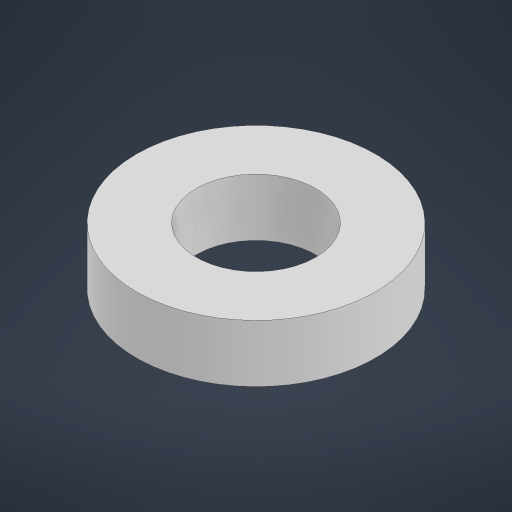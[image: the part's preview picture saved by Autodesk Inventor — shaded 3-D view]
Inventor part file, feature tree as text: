
AUTODESK INVENTOR PART (.ipt)
format: ipt  version: 2024 (Build 280153000, 153)  size: 400,896 bytes
history: native  units: mm
features: other x1, extrude x1, sketch x1
ambient origin geometry x8: Origin, YZ Plane, XZ Plane, XY Plane, X Axis, Y Axis, Z Axis, Center Point
bodies: Body1 (feature_tree)
feature tree (3):
  other  "솔리드1"
  extrude  "돌출1"  Depth=10.0mm
  sketch  "스케치1"
